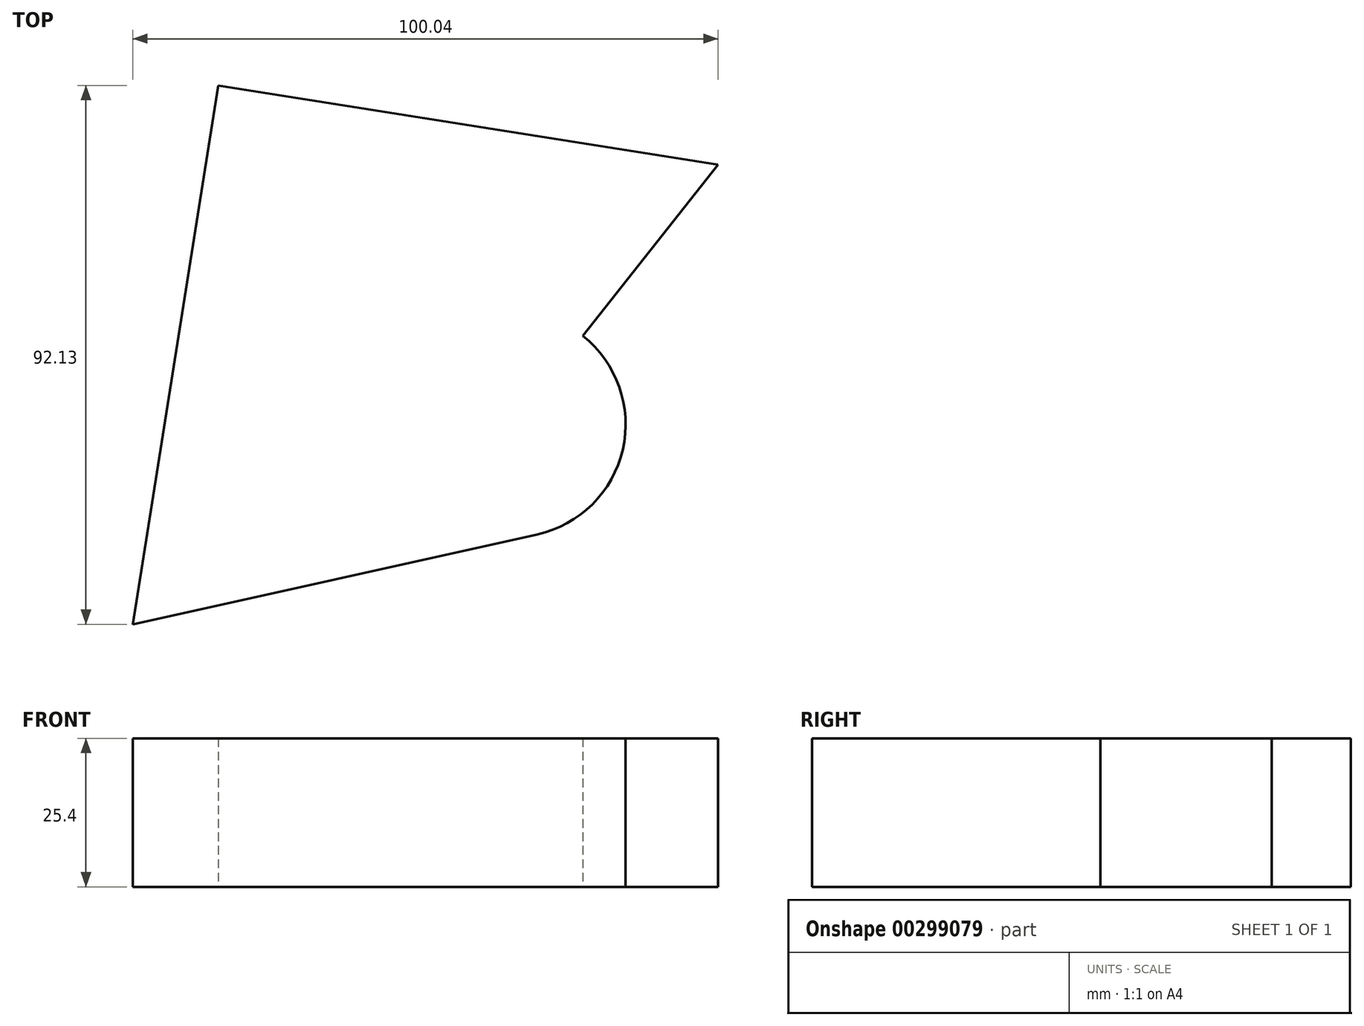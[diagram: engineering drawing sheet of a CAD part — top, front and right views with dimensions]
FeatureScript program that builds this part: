
annotation { "Feature Type Name" : "Feature", "Feature Type Description" : "" }
export const myFeature = defineFeature(function(context is Context, id is Id, definition is map)
    precondition{}
    {
        {
            var Q0;
            Q0=qCreatedBy(makeId("Top.planeOp"),FACE);
            var sketch = newSketch(context, id + "F0", { "sketchPlane" : qUnion([Q0])});
            skLineSegment(sketch, "E0", {"start": v(0, 0) * mm, "end": v(35.1, 44.41) * mm});
            skLineSegment(sketch, "E1", {"start": v(35.1, 44.41) * mm, "end": v(-50.34, 57.95) * mm});
            skLineSegment(sketch, "E2", {"start": v(-50.34, 57.95) * mm, "end": v(-64.93, -34.18) * mm});
            skLineSegment(sketch, "E3", {"start": v(-64.93, -34.18) * mm, "end": v(61.62, -6.06) * mm});
            skLineSegment(sketch, "E4", {"start": v(61.62, -6.06) * mm, "end": v(17.55, 22.2) * mm});
            skCircle(sketch, "E5", {"center": v(0, 0) * mm, "radius": 19.28 * mm});
            skLineSegment(sketch, "E6", {"start": v(61.62, -6.06) * mm, "end": v(61.62, 55.13) * mm, "construction": true});
            skSolve(sketch);
        }
        {
            var Q0;
            {var subQ0=sQuery(id+"F0.wireOp",EDGE,"E5");var subQ1=makeQuery(id+"F0.imprint","INTERSECT",VERTEX,{"derivedFrom":[sQuery(id+"F0.wireOp",EDGE,"E0"),subQ0]});Q0=makeQuery(id+"F0.imprint","IMPRINT",FACE,{"disambiguationData":[TD([[makeQuery(id+"F0.imprint","IMPRINT",EDGE,{"disambiguationData":[TD([[subQ1,-1.0]])],"derivedFrom":subQ0}),1.0]])]});}
            var Q1;
            {var subQ1=sQuery(id+"F0.wireOp",EDGE,"E1");Q1=makeQuery(id+"F0.imprint","IMPRINT",FACE,{"disambiguationData":[TD([[makeQuery(id+"F0.imprint","IMPRINT",EDGE,{"derivedFrom":subQ1}),1.0]])]});}
            extrude(context, id + "F1", {"entities" : qUnion([Q0, Q1]), "depth" : 25.4 * mm});
        }
        {
            var Q0;
            {var subQ0=sQuery(id+"F0.wireOp",EDGE,"E4");Q0=makeQuery(id+"F0.imprint","IMPRINT",FACE,{"disambiguationData":[TD([[makeQuery(id+"F0.imprint","IMPRINT",EDGE,{"derivedFrom":subQ0}),1.0]])]});}
            var Q1;
            Q1=sQuery(id+"F0.wireOp",EDGE,"E4");
            var Q2;
            Q2=sQuery(id+"F0.wireOp",EDGE,"E3");
            extrude(context, id + "F2", {"entities" : qUnion([Q0]), "bodyType" : ToolBodyType.SURFACE, "surfaceEntities" : qUnion([Q1, Q2]), "depth" : 25.4 * mm});
        }
    });
